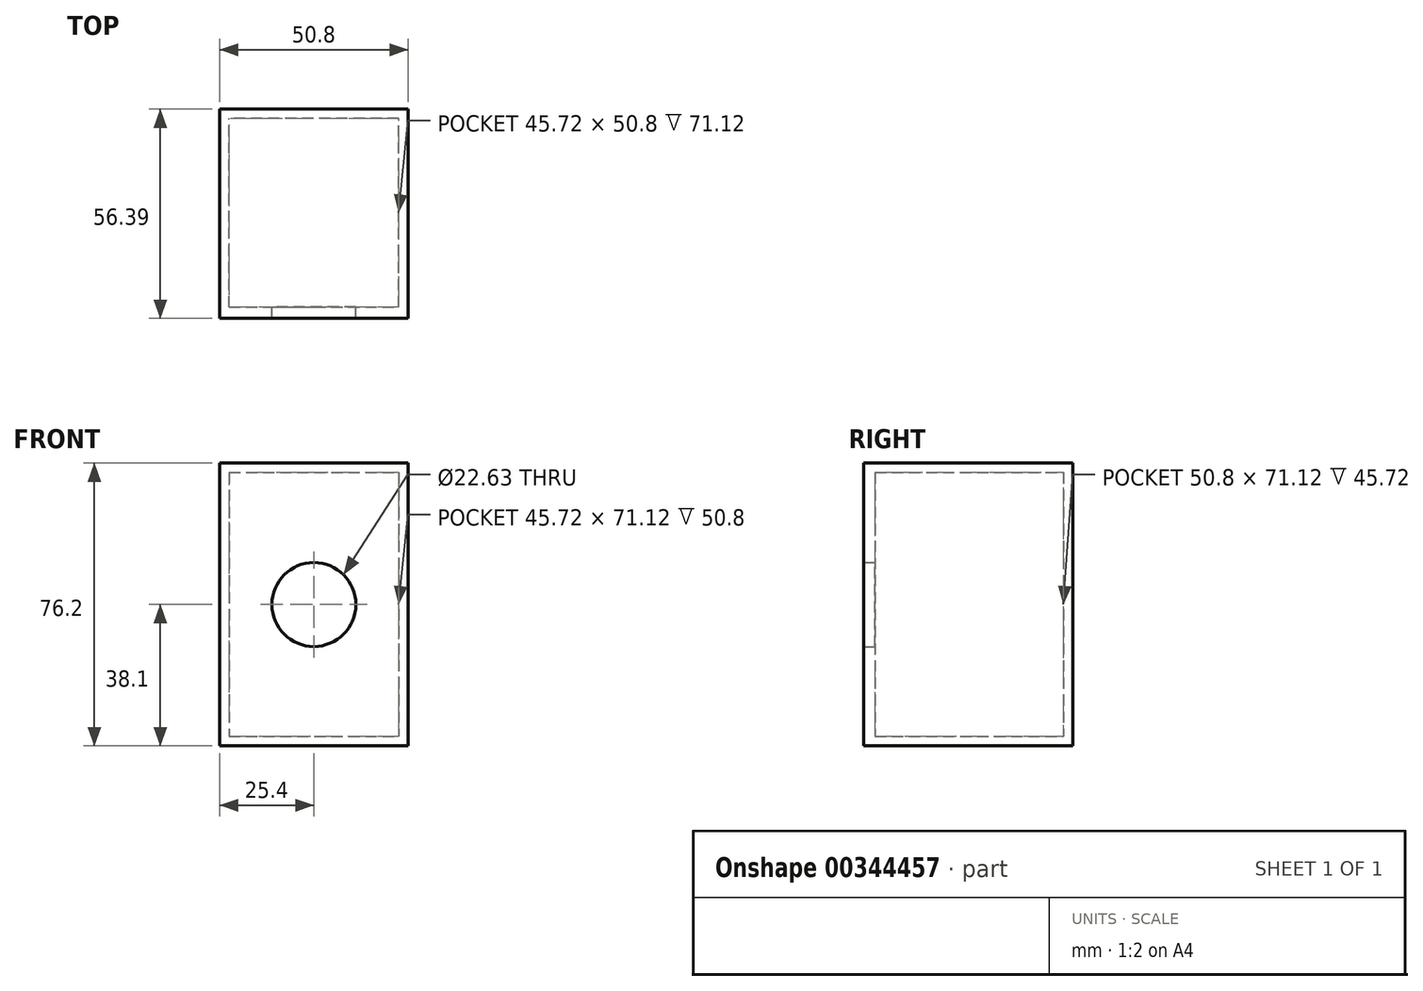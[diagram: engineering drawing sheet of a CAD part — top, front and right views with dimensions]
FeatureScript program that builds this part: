
annotation { "Feature Type Name" : "Feature", "Feature Type Description" : "" }
export const myFeature = defineFeature(function(context is Context, id is Id, definition is map)
    precondition{}
    {
        {
            var Q0;
            Q0=qCreatedBy(makeId("Front.planeOp"),FACE);
            var sketch = newSketch(context, id + "F0", { "sketchPlane" : qUnion([Q0])});
            skLineSegment(sketch, "E0.bottom", {"start": v(-25.4, 38.1) * mm, "end": v(25.4, 38.1) * mm});
            skLineSegment(sketch, "E0.top", {"start": v(-25.4, -38.1) * mm, "end": v(25.4, -38.1) * mm});
            skLineSegment(sketch, "E0.left", {"start": v(-25.4, 38.1) * mm, "end": v(-25.4, -38.1) * mm});
            skLineSegment(sketch, "E0.right", {"start": v(25.4, 38.1) * mm, "end": v(25.4, -38.1) * mm});
            skPoint(sketch, "E0.middle", {"position": v(0, 0) * mm});
            skSolve(sketch);
        }
        {
            var Q0;
            Q0=qCreatedBy(makeId("Front.planeOp"),FACE);
            cPlane(context, id + "F1", {"entities" : qUnion([Q0]), "cplaneType" : CPlaneType.OFFSET, "offset" : 50.8 * mm, "width" : 152.4 * mm, "height" : 152.4 * mm});
        }
        {
            var Q0;
            Q0=makeQuery(id+"F0.imprint","IMPRINT",FACE,{"disambiguationData":[TD([[makeQuery(id+"F0.imprint","IMPRINT",EDGE,{"derivedFrom":sQuery(id+"F0.wireOp",EDGE,"E0.bottom")}),-1.0]])]});
            extrude(context, id + "F2", {"entities" : qUnion([Q0]), "depth" : 50.8 * mm});
        }
        {
            var Q0;
            Q0=qCreatedBy(makeId("Front.planeOp"),FACE);
            var sketch = newSketch(context, id + "F3", { "sketchPlane" : qUnion([Q0])});
            skLineSegment(sketch, "E1.bottom", {"start": v(25.4, 38.1) * mm, "end": v(-25.4, 38.1) * mm});
            skLineSegment(sketch, "E1.top", {"start": v(25.4, -38.1) * mm, "end": v(-25.4, -38.1) * mm});
            skLineSegment(sketch, "E1.left", {"start": v(25.4, 38.1) * mm, "end": v(25.4, -38.1) * mm});
            skLineSegment(sketch, "E1.right", {"start": v(-25.4, 38.1) * mm, "end": v(-25.4, -38.1) * mm});
            skPoint(sketch, "E1.middle", {"position": v(0, 0) * mm});
            skSolve(sketch);
        }
        {
            var Q0;
            Q0 = qSketchRegion(id + "F3", true);
            extrude(context, id + "F4", {"entities" : qUnion([Q0]), "operationType" : NewBodyOperationType.ADD, "oppositeDirection" : true, "depth" : 2.54 * mm});
        }
        {
            var Q0;
            Q0=makeQuery(id+"F2.opExtrude","CAP_FACE",FACE,{"disambiguationData":[OSD([sQuery(id+"F0.wireOp",EDGE,"E0.bottom"),sQuery(id+"F0.wireOp",EDGE,"E0.top"),sQuery(id+"F0.wireOp",EDGE,"E0.left"),sQuery(id+"F0.wireOp",EDGE,"E0.right")])],"isStart":false});
            shell(context, id + "F5", {"entities" : qUnion([Q0]), "thickness" : 2.54 * mm});
        }
        {
            var Q0;
            Q0=qCreatedBy(id+"F1.planeOp",FACE);
            var sketch = newSketch(context, id + "F6", { "sketchPlane" : qUnion([Q0])});
            skLineSegment(sketch, "E2.0", {"start": v(-22.86, 35.56) * mm, "end": v(22.86, 35.56) * mm});
            skLineSegment(sketch, "E2.1", {"start": v(-22.86, -35.56) * mm, "end": v(22.86, -35.56) * mm});
            skLineSegment(sketch, "E2.2", {"start": v(-22.86, 35.56) * mm, "end": v(-22.86, -35.56) * mm});
            skLineSegment(sketch, "E2.3", {"start": v(22.86, 35.56) * mm, "end": v(22.86, -35.56) * mm});
            skLineSegment(sketch, "E2.4", {"start": v(25.4, 38.1) * mm, "end": v(25.4, -38.1) * mm});
            skLineSegment(sketch, "E2.5", {"start": v(-25.4, 38.1) * mm, "end": v(-25.4, -38.1) * mm});
            skLineSegment(sketch, "E2.6", {"start": v(-25.4, -38.1) * mm, "end": v(25.4, -38.1) * mm});
            skLineSegment(sketch, "E2.7", {"start": v(-25.4, 38.1) * mm, "end": v(25.4, 38.1) * mm});
            skCircle(sketch, "E3", {"center": v(0, 0) * mm, "radius": 11.31 * mm});
            skSolve(sketch);
        }
        {
            var Q0;
            Q0=makeQuery(id+"F6.imprint","IMPRINT",FACE,{"disambiguationData":[TD([[makeQuery(id+"F6.imprint","IMPRINT",EDGE,{"derivedFrom":sQuery(id+"F6.wireOp",EDGE,"E2.0")}),1.0]])]});
            var Q1;
            Q1=makeQuery(id+"F6.imprint","IMPRINT",FACE,{"disambiguationData":[TD([[makeQuery(id+"F6.imprint","IMPRINT",EDGE,{"derivedFrom":sQuery(id+"F6.wireOp",EDGE,"E2.0")}),-1.0]])]});
            extrude(context, id + "F7", {"entities" : qUnion([Q0, Q1]), "operationType" : NewBodyOperationType.ADD, "depth" : 3.05 * mm});
        }
        {
            var Q0;
            Q0=qCreatedBy(makeId("Front.planeOp"),FACE);
            cPlane(context, id + "F8", {"entities" : qUnion([Q0]), "cplaneType" : CPlaneType.OFFSET, "offset" : 2.8 * mm, "oppositeDirection" : true, "width" : 152.4 * mm, "height" : 152.4 * mm});
        }
    });
